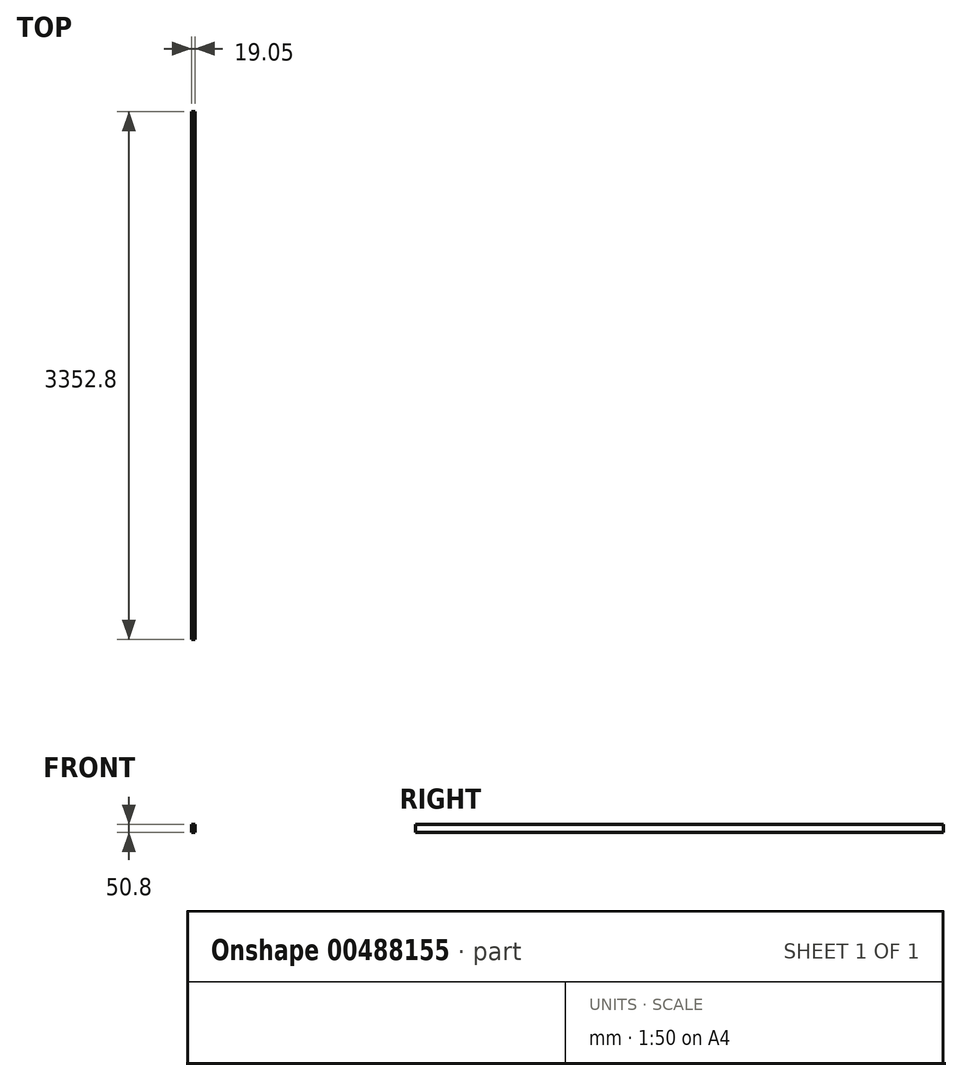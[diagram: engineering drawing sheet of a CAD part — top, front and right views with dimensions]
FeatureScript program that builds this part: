
annotation { "Feature Type Name" : "Feature", "Feature Type Description" : "" }
export const myFeature = defineFeature(function(context is Context, id is Id, definition is map)
    precondition{}
    {
        {
            var Q0;
            Q0=qCreatedBy(makeId("Front.planeOp"),FACE);
            var sketch = newSketch(context, id + "F0", { "sketchPlane" : qUnion([Q0])});
            skLineSegment(sketch, "E0", {"start": v(0, 0) * mm, "end": v(19.05, 0) * mm});
            skLineSegment(sketch, "E1", {"start": v(0, 0) * mm, "end": v(0, -50.8) * mm});
            skLineSegment(sketch, "E2", {"start": v(0, -50.8) * mm, "end": v(19.05, -50.8) * mm});
            skLineSegment(sketch, "E3", {"start": v(19.05, -50.8) * mm, "end": v(19.05, 0) * mm});
            skSolve(sketch);
        }
        {
            var Q0;
            Q0=makeQuery(id+"F0.imprint","IMPRINT",FACE,{"disambiguationData":[TD([[makeQuery(id+"F0.imprint","IMPRINT",EDGE,{"derivedFrom":sQuery(id+"F0.wireOp",EDGE,"E0")}),-1.0]])]});
            extrude(context, id + "F1", {"entities" : qUnion([Q0]), "depth" : 3352.8 * mm, "offsetDistance" : 25.4 * mm});
        }
    });
